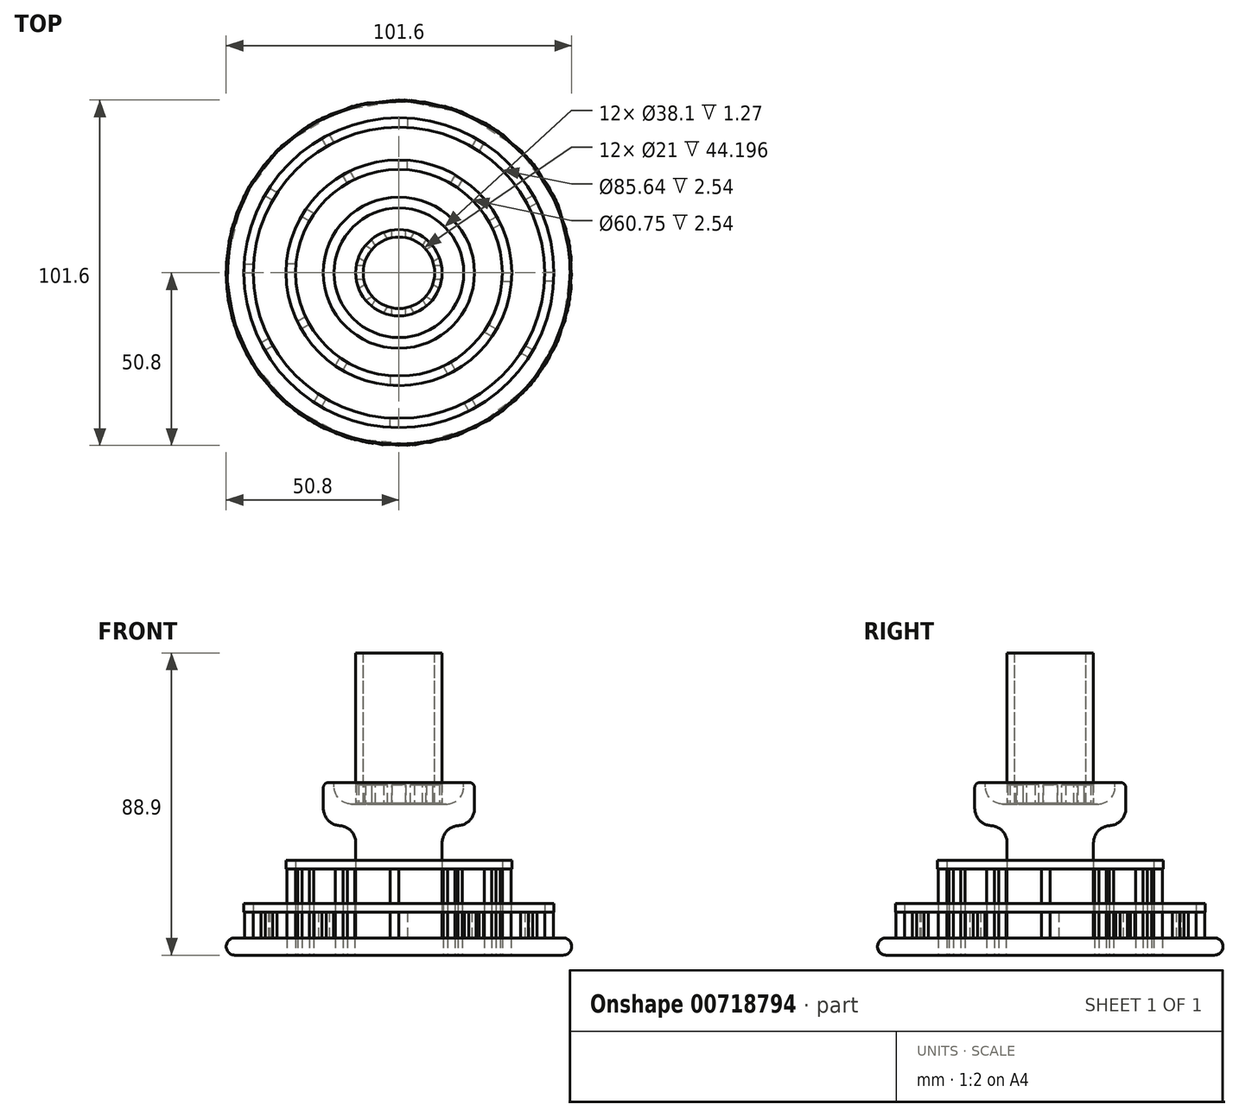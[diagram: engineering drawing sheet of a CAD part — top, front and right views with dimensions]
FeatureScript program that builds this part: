
annotation { "Feature Type Name" : "Feature", "Feature Type Description" : "" }
export const myFeature = defineFeature(function(context is Context, id is Id, definition is map)
    precondition{}
    {
        {
            var Q0;
            Q0=qCreatedBy(makeId("Top.planeOp"),FACE);
            var sketch = newSketch(context, id + "F0", { "sketchPlane" : qUnion([Q0])});
            skCircle(sketch, "E0", {"center": v(0, 0) * mm, "radius": 50.8 * mm});
            skSolve(sketch);
        }
        {
            var Q0;
            Q0=qSketchRegion(id+"F0",true);
            extrude(context, id + "F1", {"entities" : qUnion([Q0]), "depth" : 5.08 * mm, "offsetDistance" : 25.4 * mm});
        }
        {
            var Q0;
            Q0=makeQuery(id+"F1.opExtrude","SWEPT_FACE",FACE,{"disambiguationData":[OSD([sQuery(id+"F0.wireOp",EDGE,"E0")])]});
            fillet(context, id + "F2", {"entities" : qUnion([Q0]), "radius" : 2.54 * mm, "tangentPropagation" : true, "allowEdgeOverflow" : false});
        }
        {
            var Q0;
            Q0=qCreatedBy(makeId("Top.planeOp"),FACE);
            var sketch = newSketch(context, id + "F3", { "sketchPlane" : qUnion([Q0])});
            skCircle(sketch, "E1", {"center": v(0, 0) * mm, "radius": 12.7 * mm});
            skSolve(sketch);
        }
        {
            var Q0;
            Q0=qSketchRegion(id+"F3",true);
            extrude(context, id + "F4", {"entities" : qUnion([Q0]), "operationType" : NewBodyOperationType.ADD, "depth" : 88.9 * mm, "offsetDistance" : 25.4 * mm});
        }
        {
            var Q0;
            Q0=qCreatedBy(makeId("Top.planeOp"),FACE);
            var sketch = newSketch(context, id + "F5", { "sketchPlane" : qUnion([Q0])});
            skCircle(sketch, "E2", {"center": v(0, 0) * mm, "radius": 22.23 * mm});
            skSolve(sketch);
        }
        {
            var Q0;
            Q0=qSketchRegion(id+"F5",true);
            extrude(context, id + "F6", {"entities" : qUnion([Q0]), "operationType" : NewBodyOperationType.ADD, "depth" : 50.8 * mm, "offsetDistance" : 25.4 * mm, "hasSecondDirection" : true, "secondDirectionOppositeDirection" : false, "secondDirectionDepth" : 38.1 * mm});
        }
        {
            var Q0;
            Q0=makeQuery(id+"F6.opExtrude","CAP_EDGE",EDGE,{"disambiguationData":[OSD([sQuery(id+"F5.wireOp",EDGE,"E2")])],"isStart":true});
            fillet(context, id + "F7", {"entities" : qUnion([Q0]), "radius" : 5.08 * mm, "tangentPropagation" : true, "allowEdgeOverflow" : false});
        }
        {
            var Q0;
            Q0=makeQuery(id+"F6.opExtrude","CAP_FACE",FACE,{"disambiguationData":[OSD([sQuery(id+"F5.wireOp",EDGE,"E2")])],"isStart":false});
            var sketch = newSketch(context, id + "F8", { "sketchPlane" : qUnion([Q0])});
            skCircle(sketch, "E3", {"center": v(0, 0) * mm, "radius": 12.7 * mm});
            skCircle(sketch, "E4", {"center": v(0, 0) * mm, "radius": 19.05 * mm});
            skSolve(sketch);
        }
        {
            var Q0;
            Q0=qSketchRegion(id+"F8",true);
            extrude(context, id + "F9", {"entities" : qUnion([Q0]), "operationType" : NewBodyOperationType.REMOVE, "oppositeDirection" : true, "depth" : 6.35 * mm, "offsetDistance" : 25.4 * mm});
        }
        {
            var Q0;
            Q0=makeQuery(id+"F9.boolean.opBoolean","COPY",EDGE,{"derivedFrom":makeQuery(id+"F9.opExtrude","CAP_EDGE",EDGE,{"disambiguationData":[OSD([sQuery(id+"F8.wireOp",EDGE,"E4")])],"isStart":false})});
            fillet(context, id + "F10", {"entities" : qUnion([Q0]), "radius" : 5.08 * mm, "tangentPropagation" : true, "allowEdgeOverflow" : false});
        }
        {
            var Q0;
            Q0=qCreatedBy(makeId("Right.planeOp"),FACE);
            var sketch = newSketch(context, id + "F11", { "sketchPlane" : qUnion([Q0])});
            skLineSegment(sketch, "E5.right", {"start": v(-2.05, 44.7) * mm, "end": v(-2.05, 50.1) * mm});
            skLineSegment(sketch, "E6.MirrorCS", {"start": v(2.05, 44.7) * mm, "end": v(2.05, 50.1) * mm});
            skLineSegment(sketch, "E7", {"start": v(2.05, 50.1) * mm, "end": v(-2.05, 50.1) * mm});
            skLineSegment(sketch, "E8", {"start": v(2.05, 44.7) * mm, "end": v(-2.05, 44.7) * mm});
            skSolve(sketch);
        }
        {
            var Q0;
            Q0=qSketchRegion(id+"F11",true);
            extrude(context, id + "F12", {"entities" : qUnion([Q0]), "operationType" : NewBodyOperationType.REMOVE, "depth" : 12.7 * mm, "offsetDistance" : 25.4 * mm, "hasSecondDirection" : true, "secondDirectionOppositeDirection" : true, "secondDirectionDepth" : 12.7 * mm});
        }
        {
            var Q0;
            Q0=makeQuery(id+"F4.opExtrude","CAP_FACE",FACE,{"disambiguationData":[OSD([sQuery(id+"F3.wireOp",EDGE,"E1")])],"isStart":false});
            var sketch = newSketch(context, id + "F13", { "sketchPlane" : qUnion([Q0])});
            skCircle(sketch, "E9", {"center": v(0, 0) * mm, "radius": 10.5 * mm});
            skSolve(sketch);
        }
        {
            var Q0;
            Q0=qSketchRegion(id+"F13",true);
            extrude(context, id + "F14", {"entities" : qUnion([Q0]), "operationType" : NewBodyOperationType.REMOVE, "oppositeDirection" : true, "depth" : 44.2 * mm, "offsetDistance" : 25.4 * mm});
        }
        {
            var Q0;
            Q0=makeQuery(id+"F9.boolean.opBoolean","COPY",EDGE,{"derivedFrom":makeQuery(id+"F9.opExtrude","CAP_EDGE",EDGE,{"disambiguationData":[OSD([sQuery(id+"F8.wireOp",EDGE,"E4")])],"isStart":true})});
            var Q1;
            Q1=makeQuery(id+"F6.opExtrude","CAP_EDGE",EDGE,{"disambiguationData":[OSD([sQuery(id+"F5.wireOp",EDGE,"E2")])],"isStart":false});
            fillet(context, id + "F15", {"entities" : qUnion([Q0, Q1]), "radius" : 1.57 * mm, "tangentPropagation" : true, "allowEdgeOverflow" : false});
        }
        {
            var Q0;
            Q0=makeQuery(id+"F6.boolean.opBoolean","INTERSECT",EDGE,{"derivedFrom":[makeQuery(id+"F4.opExtrude","SWEPT_FACE",FACE,{"disambiguationData":[OSD([sQuery(id+"F3.wireOp",EDGE,"E1")])]}),makeQuery(id+"F6.opExtrude","CAP_FACE",FACE,{"disambiguationData":[OSD([sQuery(id+"F5.wireOp",EDGE,"E2")])],"isStart":true})]});
            fillet(context, id + "F16", {"entities" : qUnion([Q0]), "radius" : 5.08 * mm, "tangentPropagation" : true, "allowEdgeOverflow" : false});
        }
        {
            var Q0;
            Q0=qCreatedBy(makeId("Front.planeOp"),FACE);
            var sketch = newSketch(context, id + "F17", { "sketchPlane" : qUnion([Q0])});
            skLineSegment(sketch, "E10", {"start": v(0, 0) * mm, "end": v(0, 97) * mm, "construction": true});
            skSolve(sketch);
        }
        {
            var Q0;
            Q0=qCreatedBy(makeId("Top.planeOp"),FACE);
            var sketch = newSketch(context, id + "F18", { "sketchPlane" : qUnion([Q0])});
            skLineSegment(sketch, "E11.bottom", {"start": v(30.38, 0) * mm, "end": v(32.92, 0) * mm});
            skLineSegment(sketch, "E11.top", {"start": v(30.38, -2.54) * mm, "end": v(32.92, -2.54) * mm});
            skLineSegment(sketch, "E11.left", {"start": v(30.38, 0) * mm, "end": v(30.38, -2.54) * mm});
            skLineSegment(sketch, "E11.right", {"start": v(32.92, 0) * mm, "end": v(32.92, -2.54) * mm});
            skSolve(sketch);
        }
        {
            var Q0;
            Q0 = qSketchRegion(id + "F18", true);
            extrude(context, id + "F19", {"entities" : qUnion([Q0]), "depth" : 25.4 * mm, "offsetDistance" : 25.4 * mm, "hasSecondDirection" : true, "secondDirectionOppositeDirection" : true, "secondDirectionDepth" : 0 * mm});
        }
        {
            var Q0;
            Q0=qCreatedBy(makeId("Top.planeOp"),FACE);
            var sketch = newSketch(context, id + "F20", { "sketchPlane" : qUnion([Q0])});
            skLineSegment(sketch, "E12.bottom", {"start": v(42.84, 0) * mm, "end": v(45.38, 0) * mm});
            skLineSegment(sketch, "E12.top", {"start": v(42.84, -2.54) * mm, "end": v(45.38, -2.54) * mm});
            skLineSegment(sketch, "E12.left", {"start": v(42.84, 0) * mm, "end": v(42.84, -2.54) * mm});
            skLineSegment(sketch, "E12.right", {"start": v(45.38, 0) * mm, "end": v(45.38, -2.54) * mm});
            skSolve(sketch);
        }
        {
            var Q0;
            Q0 = qSketchRegion(id + "F20", true);
            extrude(context, id + "F21", {"entities" : qUnion([Q0]), "operationType" : NewBodyOperationType.ADD, "depth" : 12.7 * mm, "offsetDistance" : 25.4 * mm});
        }
        {
            var Q0;
            Q0=makeQuery(id+"F1.opExtrude","SWEPT_BODY",BODY,{"disambiguationData":[OSD([sQuery(id+"F0.wireOp",EDGE,"E0")])]});
            var Q1;
            Q1=makeQuery(id+"F19.opExtrude","SWEPT_BODY",BODY,{"disambiguationData":[OSD([sQuery(id+"F18.wireOp",EDGE,"E11.bottom"),sQuery(id+"F18.wireOp",EDGE,"E11.top"),sQuery(id+"F18.wireOp",EDGE,"E11.left"),sQuery(id+"F18.wireOp",EDGE,"E11.right")])]});
            var Q2;
            Q2=sQuery(id+"F17.wireOp",EDGE,"E10");
            circularPattern(context, id + "F22", {"entities" : qUnion([Q0, Q1]), "axis" : qUnion([Q2]), "angle" : 360 * degree, "instanceCount" : 12, "equalSpace" : true});
        }
        {
            var Q0;
            Q0=qCreatedBy(makeId("Top.planeOp"),FACE);
            var sketch = newSketch(context, id + "F23", { "sketchPlane" : qUnion([Q0])});
            skCircle(sketch, "E13", {"center": v(0, 0) * mm, "radius": 30.38 * mm});
            skCircle(sketch, "E14", {"center": v(0, 0) * mm, "radius": 33.2 * mm});
            skSolve(sketch);
        }
        {
            var Q0;
            Q0 = qSketchRegion(id + "F23", true);
            extrude(context, id + "F24", {"entities" : qUnion([Q0]), "depth" : 27.94 * mm, "offsetDistance" : 25.4 * mm, "hasSecondDirection" : true, "secondDirectionOppositeDirection" : false, "secondDirectionDepth" : 25.4 * mm});
        }
        {
            var Q0;
            Q0=qCreatedBy(makeId("Top.planeOp"),FACE);
            var sketch = newSketch(context, id + "F25", { "sketchPlane" : qUnion([Q0])});
            skCircle(sketch, "E15", {"center": v(0, 0) * mm, "radius": 42.82 * mm});
            skCircle(sketch, "E16", {"center": v(0, 0) * mm, "radius": 45.58 * mm});
            skSolve(sketch);
        }
        {
            var Q0;
            Q0 = qSketchRegion(id + "F25", true);
            extrude(context, id + "F26", {"entities" : qUnion([Q0]), "depth" : 15.24 * mm, "offsetDistance" : 25.4 * mm, "hasSecondDirection" : true, "secondDirectionOppositeDirection" : false, "secondDirectionDepth" : 12.7 * mm});
        }
    });
